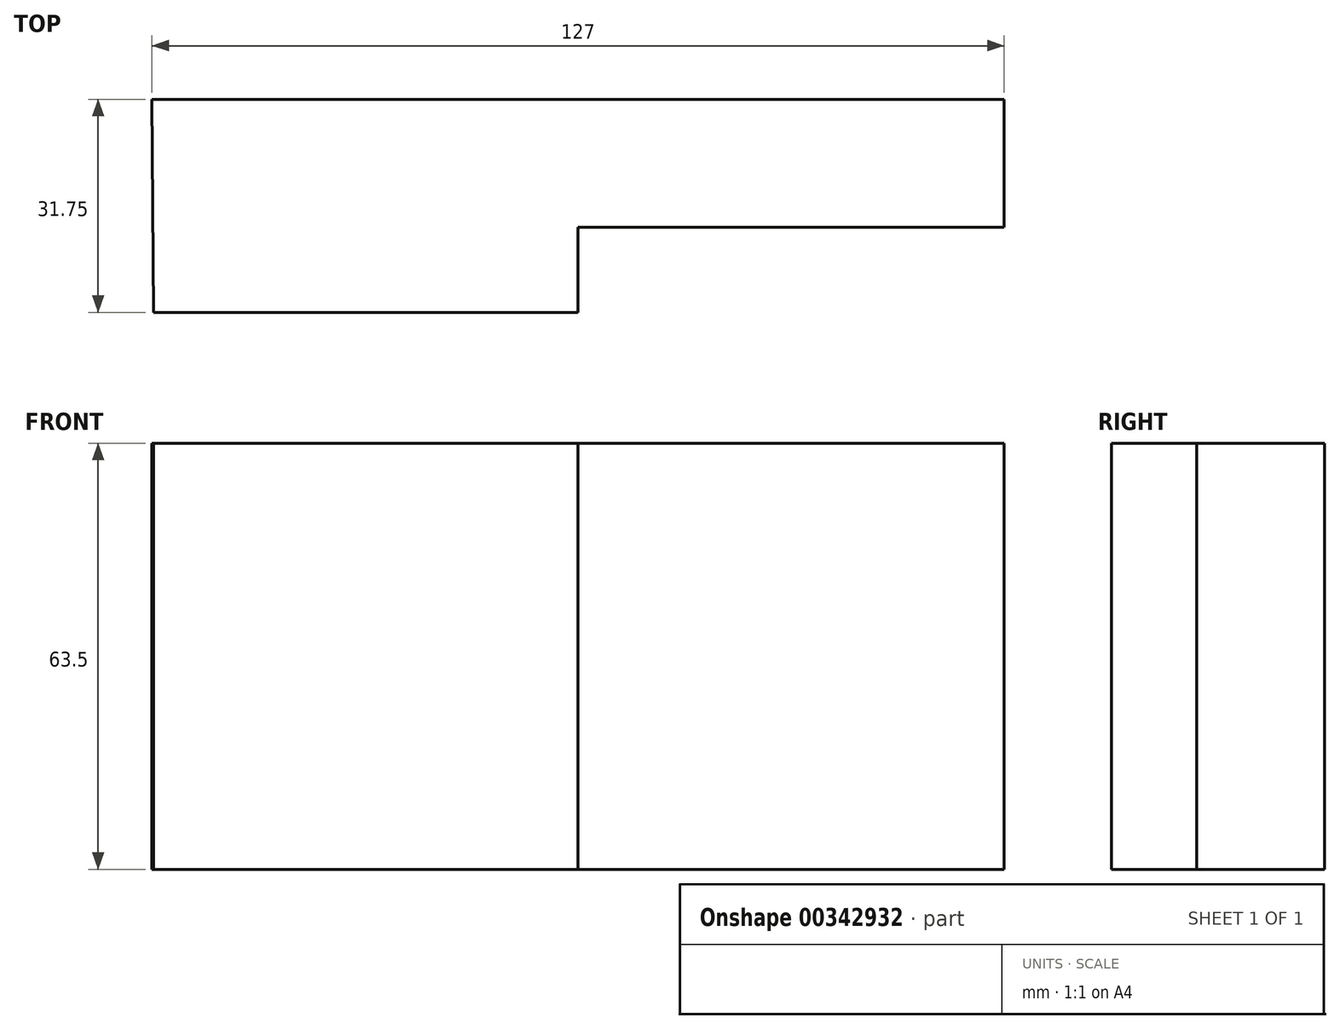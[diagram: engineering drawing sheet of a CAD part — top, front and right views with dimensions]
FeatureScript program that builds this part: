
annotation { "Feature Type Name" : "Feature", "Feature Type Description" : "" }
export const myFeature = defineFeature(function(context is Context, id is Id, definition is map)
    precondition{}
    {
        {
            var Q0;
            Q0=qCreatedBy(makeId("Top.planeOp"),FACE);
            var sketch = newSketch(context, id + "F0", { "sketchPlane" : qUnion([Q0])});
            skLineSegment(sketch, "E0", {"start": v(-65.83, 31.75) * mm, "end": v(61.17, 31.75) * mm});
            skLineSegment(sketch, "E1", {"start": v(61.17, 31.75) * mm, "end": v(61.17, 12.7) * mm});
            skLineSegment(sketch, "E2", {"start": v(61.17, 12.7) * mm, "end": v(-2.33, 12.7) * mm});
            skLineSegment(sketch, "E3", {"start": v(-2.33, 12.7) * mm, "end": v(15.45, 12.7) * mm});
            skLineSegment(sketch, "E4", {"start": v(-2.33, 12.7) * mm, "end": v(-2.33, 0) * mm});
            skLineSegment(sketch, "E5", {"start": v(-2.33, 0) * mm, "end": v(-65.59, 0) * mm});
            skLineSegment(sketch, "E6", {"start": v(-65.83, 31.75) * mm, "end": v(-65.59, 0) * mm});
            skSolve(sketch);
        }
        {
            var Q0;
            Q0 = qSketchRegion(id + "F0", true);
            extrude(context, id + "F1", {"entities" : qUnion([Q0]), "depth" : 63.5 * mm});
        }
        {
            var Q0;
            Q0 = qSketchRegion(id + "F0", true);
            extrude(context, id + "F2", {"entities" : qUnion([Q0]), "operationType" : NewBodyOperationType.ADD, "depth" : 63.5 * mm});
        }
    });
